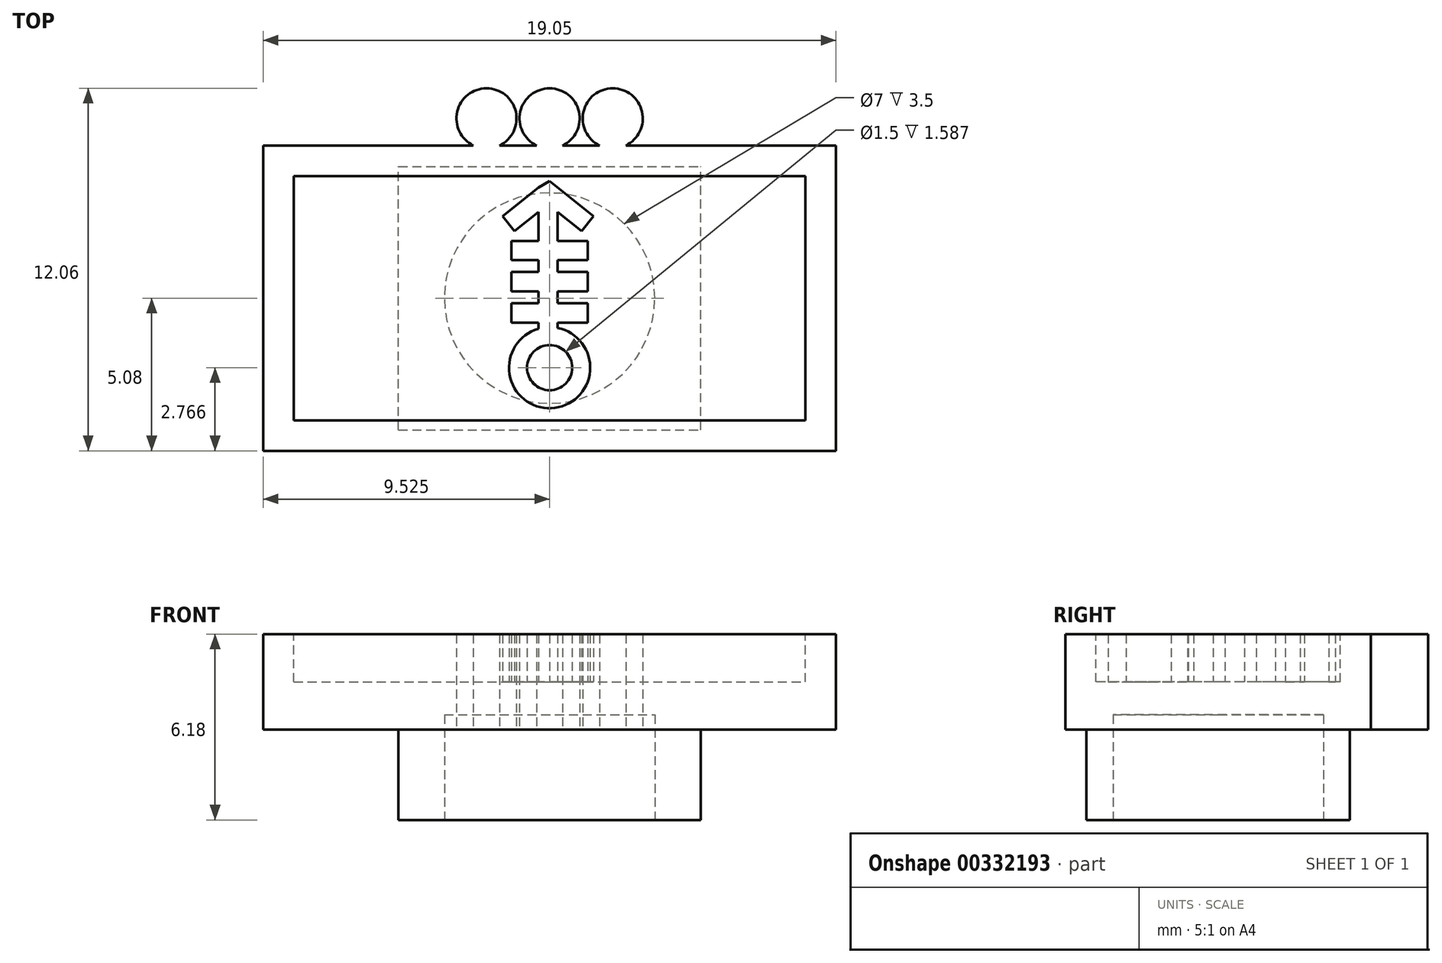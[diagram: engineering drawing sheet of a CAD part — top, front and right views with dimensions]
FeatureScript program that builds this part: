
annotation { "Feature Type Name" : "Feature", "Feature Type Description" : "" }
export const myFeature = defineFeature(function(context is Context, id is Id, definition is map)
    precondition{}
    {
        {
            var Q0;
            Q0=qCreatedBy(makeId("Top.planeOp"),FACE);
            var sketch = newSketch(context, id + "F0", { "sketchPlane" : qUnion([Q0])});
            skLineSegment(sketch, "E0.bottom", {"start": v(-19.05, 10.16) * mm, "end": v(0, 10.16) * mm});
            skLineSegment(sketch, "E0.top", {"start": v(-19.05, 0) * mm, "end": v(0, 0) * mm});
            skLineSegment(sketch, "E0.left", {"start": v(-19.05, 10.16) * mm, "end": v(-19.05, 0) * mm});
            skLineSegment(sketch, "E0.right", {"start": v(0, 10.16) * mm, "end": v(0, 0) * mm});
            skCircle(sketch, "E1", {"center": v(-9.53, 11.06) * mm, "radius": 1 * mm});
            skLineSegment(sketch, "E2", {"start": v(-9.52, 10.16) * mm, "end": v(-9.52, 0) * mm, "construction": true});
            skCircle(sketch, "E3", {"center": v(-11.62, 11.06) * mm, "radius": 1 * mm});
            skCircle(sketch, "E4.MirrorC", {"center": v(-7.43, 11.06) * mm, "radius": 1 * mm});
            skSolve(sketch);
        }
        {
            var Q0;
            Q0=qSketchRegion(id+"F0",true);
            extrude(context, id + "F1", {"entities" : qUnion([Q0]), "depth" : 3.17 * mm});
        }
        {
            var Q0;
            Q0=makeQuery(id+"F1.opExtrude","CAP_FACE",FACE,{"disambiguationData":[OSD([sQuery(id+"F0.wireOp",EDGE,"E0.bottom"),sQuery(id+"F0.wireOp",EDGE,"E0.top"),sQuery(id+"F0.wireOp",EDGE,"E0.left"),sQuery(id+"F0.wireOp",EDGE,"E0.right")])],"isStart":false});
            var sketch = newSketch(context, id + "F2", { "sketchPlane" : qUnion([Q0])});
            skLineSegment(sketch, "E5.bottom", {"start": v(-18.03, 9.14) * mm, "end": v(-1.02, 9.14) * mm});
            skLineSegment(sketch, "E5.top", {"start": v(-18.03, 1.02) * mm, "end": v(-1.02, 1.02) * mm});
            skLineSegment(sketch, "E5.left", {"start": v(-18.03, 9.14) * mm, "end": v(-18.03, 1.02) * mm});
            skLineSegment(sketch, "E5.right", {"start": v(-1.02, 9.14) * mm, "end": v(-1.02, 1.02) * mm});
            skSolve(sketch);
        }
        {
            var Q0;
            Q0=qSketchRegion(id+"F2",true);
            extrude(context, id + "F3", {"entities" : qUnion([Q0]), "operationType" : NewBodyOperationType.REMOVE, "oppositeDirection" : true, "depth" : 1.59 * mm});
        }
        {
            var Q0;
            Q0=makeQuery(id+"F1.opExtrude","CAP_FACE",FACE,{"disambiguationData":[OSD([sQuery(id+"F0.wireOp",EDGE,"E0.bottom"),sQuery(id+"F0.wireOp",EDGE,"E0.top"),sQuery(id+"F0.wireOp",EDGE,"E0.left"),sQuery(id+"F0.wireOp",EDGE,"E0.right"),sQuery(id+"F0.wireOp",EDGE,"E1"),sQuery(id+"F0.wireOp",EDGE,"E3"),sQuery(id+"F0.wireOp",EDGE,"E4.MirrorC")])],"isStart":true});
            var sketch = newSketch(context, id + "F4", { "sketchPlane" : qUnion([Q0])});
            skLineSegment(sketch, "E6.bottom", {"start": v(-14.55, -0.7) * mm, "end": v(-4.5, -0.7) * mm});
            skLineSegment(sketch, "E6.top", {"start": v(-14.55, -9.46) * mm, "end": v(-4.5, -9.46) * mm});
            skLineSegment(sketch, "E6.left", {"start": v(-14.55, -0.7) * mm, "end": v(-14.55, -9.46) * mm});
            skLineSegment(sketch, "E6.right", {"start": v(-4.5, -0.7) * mm, "end": v(-4.5, -9.46) * mm});
            skSolve(sketch);
        }
        {
            var Q0;
            Q0=qSketchRegion(id+"F4",true);
            extrude(context, id + "F5", {"entities" : qUnion([Q0]), "operationType" : NewBodyOperationType.ADD, "depth" : 3 * mm, "offsetDistance" : 25 * mm});
        }
        {
            var Q0;
            Q0=makeQuery(id+"F5.opExtrude","CAP_FACE",FACE,{"disambiguationData":[OSD([sQuery(id+"F4.wireOp",EDGE,"E6.bottom"),sQuery(id+"F4.wireOp",EDGE,"E6.top"),sQuery(id+"F4.wireOp",EDGE,"E6.left"),sQuery(id+"F4.wireOp",EDGE,"E6.right")])],"isStart":false});
            var sketch = newSketch(context, id + "F6", { "sketchPlane" : qUnion([Q0])});
            skCircle(sketch, "E7", {"center": v(-9.52, -5.08) * mm, "radius": 3.5 * mm});
            skLineSegment(sketch, "E8", {"start": v(-19.05, -5.08) * mm, "end": v(0, -5.08) * mm, "construction": true});
            skPoint(sketch, "E8.endSnap0", {"position": v(-4.5, -5.08) * mm});
            skLineSegment(sketch, "E9", {"start": v(-9.53, 0) * mm, "end": v(-9.53, -9.46) * mm, "construction": true});
            skSolve(sketch);
        }
        {
            var Q0;
            Q0=makeQuery(id+"F6.imprint","IMPRINT",FACE,{"disambiguationData":[TD([[makeQuery(id+"F6.imprint","IMPRINT",EDGE,{"derivedFrom":sQuery(id+"F6.wireOp",EDGE,"E7")}),1.0]])]});
            extrude(context, id + "F7", {"entities" : qUnion([Q0]), "operationType" : NewBodyOperationType.REMOVE, "oppositeDirection" : true, "depth" : 3.5 * mm, "offsetDistance" : 25 * mm});
        }
        {
            var Q0;
            {var subQ0=sQuery(id+"F2.wireOp",EDGE,"E5.top");var subQ1=makeQuery(id+"F3.boolean.opBoolean","COPY",FACE,{"derivedFrom":makeQuery(id+"F3.opExtrude","SWEPT_FACE",FACE,{"disambiguationData":[OSD([subQ0])]})});Q0=makeQuery(id+"FV7TiC2D1ffqNPq_1.boolean.opBoolean","SPLIT",FACE,{"disambiguationData":[TD([makeQuery(id+"FV7TiC2D1ffqNPq_1.opExtrude","SWEPT_FACE",FACE,{"disambiguationData":[OSD([sQuery(id+"F3gTNkO265XWn0P_1.wireOp",EDGE,"MWbnN6lQ-Jp35-iDjw-4vqv-6XMauFatj97d")])]})])],"derivedFrom":makeQuery(id+"FD6hazfNaiJcgqe_1.boolean.opBoolean","SPLIT",FACE,{"disambiguationData":[TD([subQ1])],"derivedFrom":makeQuery(id+"F3.boolean.opBoolean","COPY",FACE,{"derivedFrom":makeQuery(id+"F3.opExtrude","CAP_FACE",FACE,{"disambiguationData":[OSD([sQuery(id+"F2.wireOp",EDGE,"E5.bottom"),subQ0,sQuery(id+"F2.wireOp",EDGE,"E5.left"),sQuery(id+"F2.wireOp",EDGE,"E5.right")])],"isStart":false})})})});}
            var sketch = newSketch(context, id + "F8", { "sketchPlane" : qUnion([Q0])});
            skLineSegment(sketch, "E10", {"start": v(-9.52, 9.14) * mm, "end": v(-9.52, 0) * mm, "construction": true});
            skLineSegment(sketch, "E11", {"start": v(-19.05, 5.08) * mm, "end": v(0, 5.08) * mm, "construction": true});
            skCircle(sketch, "E12", {"center": v(-9.52, 2.77) * mm, "radius": 1.35 * mm});
            skLineSegment(sketch, "E13.bottom", {"start": v(-9.9, 8.76) * mm, "end": v(-9.26, 8.76) * mm});
            skLineSegment(sketch, "E13.left", {"start": v(-9.9, 8.76) * mm, "end": v(-9.9, 4.06) * mm});
            skLineSegment(sketch, "E13.right", {"start": v(-9.26, 8.76) * mm, "end": v(-9.26, 4.09) * mm});
            skLineSegment(sketch, "E14.bottom", {"start": v(-10.8, 6.99) * mm, "end": v(-8.25, 6.99) * mm});
            skLineSegment(sketch, "E14.top", {"start": v(-10.8, 6.35) * mm, "end": v(-8.25, 6.35) * mm});
            skLineSegment(sketch, "E14.left", {"start": v(-10.8, 6.99) * mm, "end": v(-10.8, 6.35) * mm});
            skLineSegment(sketch, "E14.right", {"start": v(-8.25, 6.99) * mm, "end": v(-8.25, 6.35) * mm});
            skLineSegment(sketch, "E15.bottom", {"start": v(-10.8, 5.95) * mm, "end": v(-8.25, 5.95) * mm});
            skLineSegment(sketch, "E15.top", {"start": v(-10.8, 5.3) * mm, "end": v(-8.25, 5.3) * mm});
            skLineSegment(sketch, "E15.left", {"start": v(-10.8, 5.95) * mm, "end": v(-10.8, 5.3) * mm});
            skLineSegment(sketch, "E15.right", {"start": v(-8.25, 5.95) * mm, "end": v(-8.25, 5.3) * mm});
            skLineSegment(sketch, "E16.bottom", {"start": v(-10.8, 4.9) * mm, "end": v(-8.25, 4.9) * mm});
            skLineSegment(sketch, "E16.top", {"start": v(-10.8, 4.27) * mm, "end": v(-8.25, 4.27) * mm});
            skLineSegment(sketch, "E16.left", {"start": v(-10.8, 4.9) * mm, "end": v(-10.8, 4.27) * mm});
            skLineSegment(sketch, "E16.right", {"start": v(-8.25, 4.9) * mm, "end": v(-8.25, 4.27) * mm});
            skLineSegment(sketch, "E17", {"start": v(-9.9, 8.76) * mm, "end": v(-11.09, 7.81) * mm});
            skLineSegment(sketch, "E18", {"start": v(-11.09, 7.81) * mm, "end": v(-10.7, 7.32) * mm});
            skLineSegment(sketch, "E19", {"start": v(-10.7, 7.32) * mm, "end": v(-9.9, 7.95) * mm});
            skLineSegment(sketch, "E20", {"start": v(-9.26, 8.76) * mm, "end": v(-8.07, 7.81) * mm});
            skLineSegment(sketch, "E21", {"start": v(-8.07, 7.81) * mm, "end": v(-8.47, 7.32) * mm});
            skLineSegment(sketch, "E22", {"start": v(-8.47, 7.32) * mm, "end": v(-9.26, 7.95) * mm});
            skLineSegment(sketch, "E23", {"start": v(-9.9, 8.76) * mm, "end": v(-9.52, 8.98) * mm});
            skLineSegment(sketch, "E24", {"start": v(-9.52, 8.98) * mm, "end": v(-9.26, 8.76) * mm});
            skCircle(sketch, "E25", {"center": v(-9.52, 2.77) * mm, "radius": 0.75 * mm});
            skSolve(sketch);
        }
        {
            var Q0;
            Q0=qSketchRegion(id+"F8",true);
            var Q1;
            Q1=makeQuery(id+"F1.opExtrude","CAP_FACE",FACE,{"disambiguationData":[OSD([sQuery(id+"F0.wireOp",EDGE,"E0.bottom"),sQuery(id+"F0.wireOp",EDGE,"E0.top"),sQuery(id+"F0.wireOp",EDGE,"E0.left"),sQuery(id+"F0.wireOp",EDGE,"E0.right"),sQuery(id+"F0.wireOp",EDGE,"E1"),sQuery(id+"F0.wireOp",EDGE,"E3"),sQuery(id+"F0.wireOp",EDGE,"E4.MirrorC")])],"isStart":false});
            extrude(context, id + "F9", {"entities" : qUnion([Q0]), "operationType" : NewBodyOperationType.ADD, "endBound" : BoundingType.UP_TO_SURFACE, "depth" : 25 * mm, "endBoundEntityFace" : qUnion([Q1]), "offsetDistance" : 25 * mm});
        }
    });
